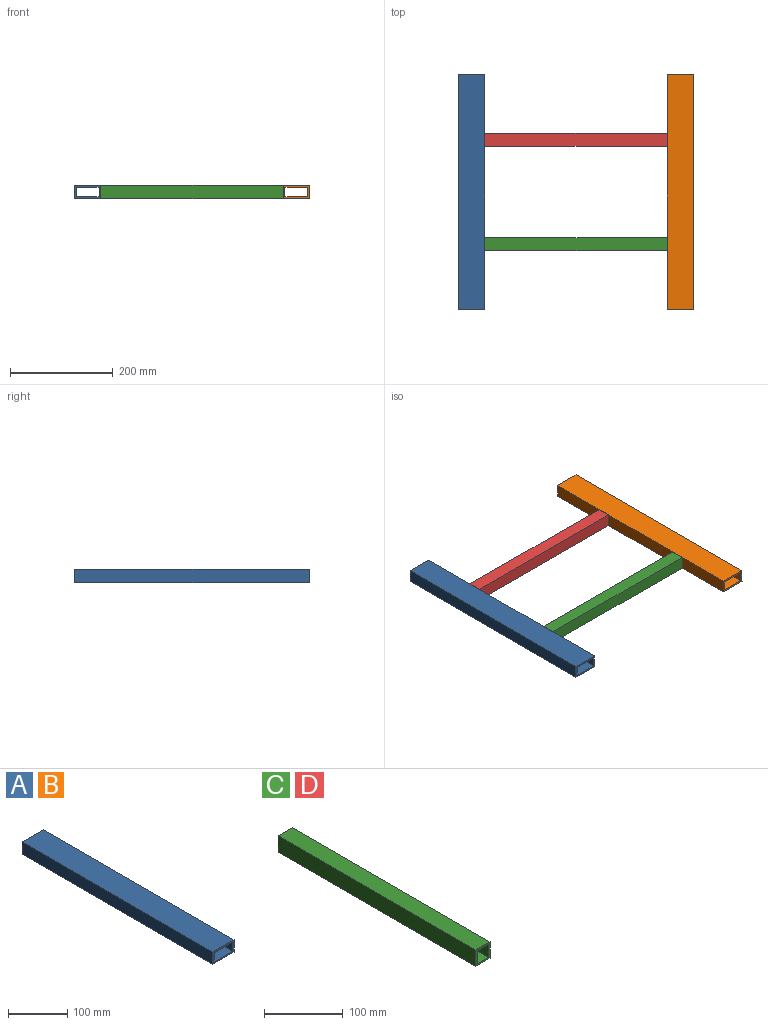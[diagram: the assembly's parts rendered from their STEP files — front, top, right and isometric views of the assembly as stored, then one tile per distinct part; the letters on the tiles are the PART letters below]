
ASSEMBLY  parts=4 mates=3
PART A: 10 faces, bbox 50.8x457.2x25.4 mm
  f0: plane 50.8x25.4mm, normal (0,1,0), area 443.5mm2, adj f2,f3,f4,f5,f6,f7,f8,f9
  f1: plane 50.8x25.4mm, normal (0,-1,0), area 443.5mm2, adj f2,f3,f4,f5,f6,f7,f8,f9
  f2: plane 457.2x25.4mm, normal (-1,0,0), area 11612.9mm2, adj f0,f1,f4,f5
  f3: plane 457.2x25.4mm, normal (1,0,0), area 11612.9mm2, adj f0,f1,f4,f5
  f4: plane 457.2x50.8mm, normal (0,0,1), area 23225.8mm2, adj f0,f1,f2,f3
  f5: plane 457.2x50.8mm, normal (0,0,-1), area 23225.8mm2, adj f0,f1,f2,f3
  f6: plane 457.2x19.05mm, normal (1,0,0), area 8709.7mm2, adj f0,f1,f8,f9
  f7: plane 457.2x19.05mm, normal (-1,0,0), area 8709.7mm2, adj f0,f1,f8,f9
  f8: plane 457.2x44.45mm, normal (0,0,-1), area 20322.5mm2, adj f0,f1,f6,f7
  f9: plane 457.2x44.45mm, normal (0,0,1), area 20322.5mm2, adj f0,f1,f6,f7
PART B: same geometry as A
PART C: 10 faces, bbox 25.4x355.6x25.4 mm
  f0: plane 25.4x25.4mm, normal (0,1,0), area 232.3mm2, adj f2,f3,f4,f5,f6,f7,f8,f9
  f1: plane 25.4x25.4mm, normal (0,-1,0), area 232.3mm2, adj f2,f3,f4,f5,f6,f7,f8,f9
  f2: plane 355.6x25.4mm, normal (-1,0,0), area 9032.2mm2, adj f0,f1,f4,f5
  f3: plane 355.6x25.4mm, normal (1,0,0), area 9032.2mm2, adj f0,f1,f4,f5
  f4: plane 355.6x25.4mm, normal (0,0,1), area 9032.2mm2, adj f0,f1,f2,f3
  f5: plane 355.6x25.4mm, normal (0,0,-1), area 9032.2mm2, adj f0,f1,f2,f3
  f6: plane 355.6x20.32mm, normal (1,0,0), area 7225.8mm2, adj f0,f1,f8,f9
  f7: plane 355.6x20.32mm, normal (-1,0,0), area 7225.8mm2, adj f0,f1,f8,f9
  f8: plane 355.6x20.32mm, normal (0,0,-1), area 7225.8mm2, adj f0,f1,f6,f7
  f9: plane 355.6x20.32mm, normal (0,0,1), area 7225.8mm2, adj f0,f1,f6,f7
PART D: same geometry as C
PLACE A rot(axis=(0.33,-0.48,-0.81),0deg) t=(-144.56,-85.97,-14.9)mm
PLACE B rot(axis=(0.33,-0.48,-0.81),0deg) t=(261.84,-85.97,-14.9)mm
PLACE C rot(axis=(-0.71,0.71,0),180deg) t=(29.45,-21.17,-2.2)mm
PLACE D rot(axis=(0,0,-1),90deg) t=(-2.33,182.03,-27.6)mm
MATE fastened B.f2 <-> D.f0  axis (-1,0,0) through (191.36,166.46,-14.9)mm
MATE fastened C.f0 <-> A.f3  axis (-1,0,0) through (-164.24,-36.74,-14.9)mm
MATE fastened D.f1 <-> A.f3  axis (-1,0,0) through (-164.24,166.46,-14.9)mm
